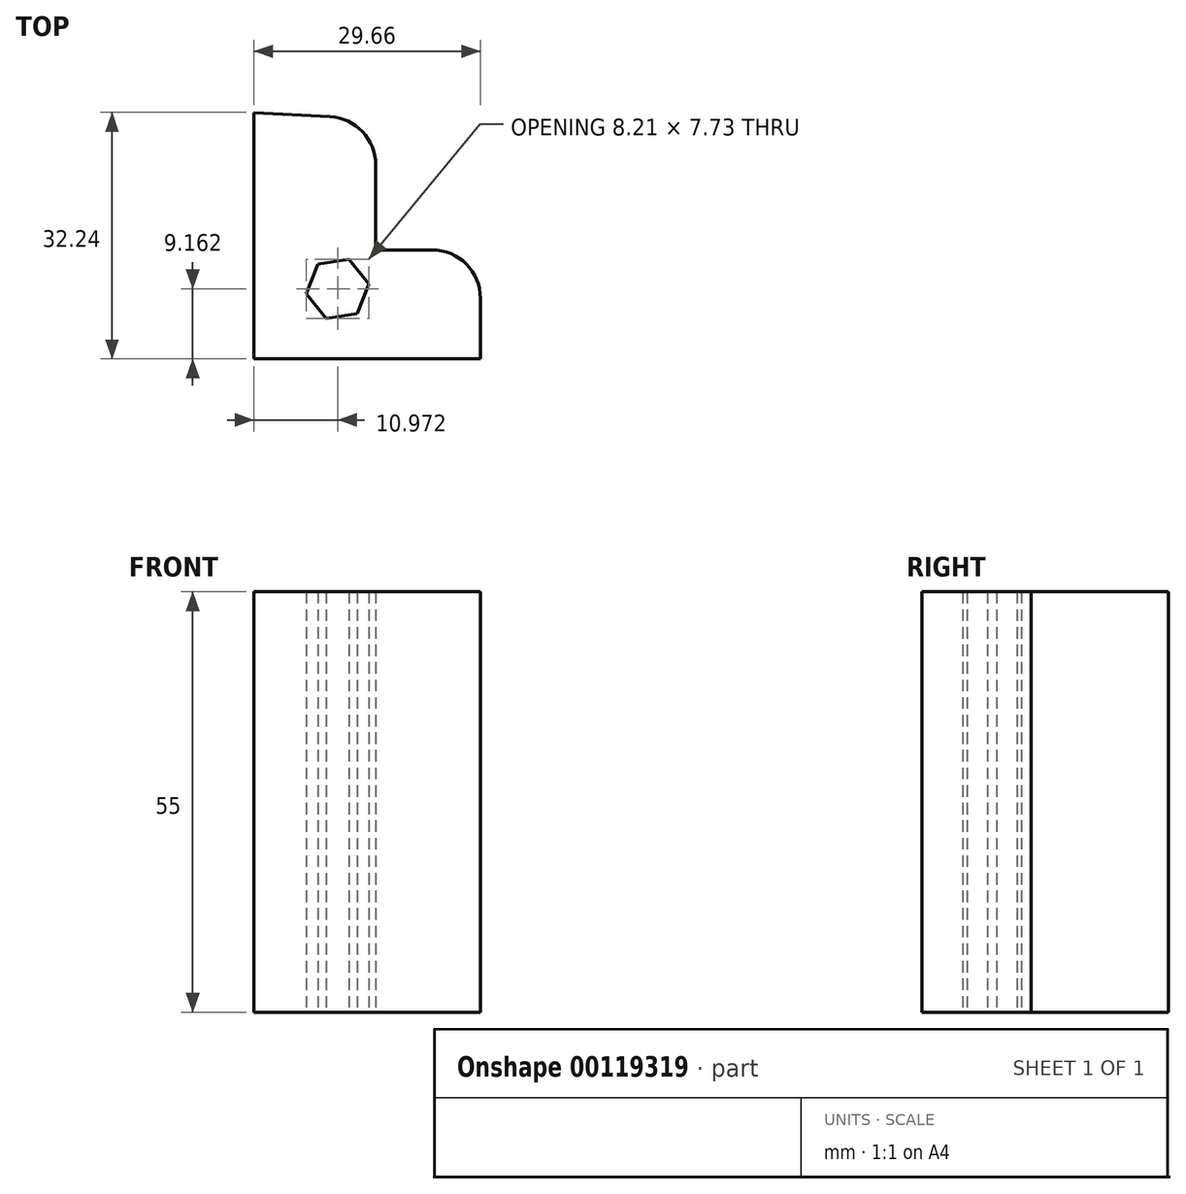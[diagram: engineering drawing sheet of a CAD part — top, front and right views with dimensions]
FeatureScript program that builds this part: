
annotation { "Feature Type Name" : "Feature", "Feature Type Description" : "" }
export const myFeature = defineFeature(function(context is Context, id is Id, definition is map)
    precondition{}
    {
        {
            var Q0;
            Q0=qCreatedBy(makeId("Top.planeOp"),FACE);
            var sketch = newSketch(context, id + "F0", { "sketchPlane" : qUnion([Q0])});
            skLineSegment(sketch, "E0", {"start": v(-55.05, 38.94) * mm, "end": v(-55.05, 6.7) * mm});
            skLineSegment(sketch, "E1", {"start": v(-55.05, 6.7) * mm, "end": v(-25.39, 6.7) * mm});
            skLineSegment(sketch, "E2", {"start": v(-25.39, 6.7) * mm, "end": v(-25.39, 14.62) * mm});
            skLineSegment(sketch, "E3", {"start": v(-31.74, 20.97) * mm, "end": v(-39.08, 20.97) * mm});
            skLineSegment(sketch, "E4", {"start": v(-39.08, 20.97) * mm, "end": v(-39.08, 32.06) * mm});
            skLineSegment(sketch, "E5", {"start": v(-45.09, 38.4) * mm, "end": v(-55.05, 38.94) * mm});
            skPoint(sketch, "E6.visualSharp", {"position": v(-39.08, 38.08) * mm});
            skArc(sketch, "E6.filletArc", {"start": v(-39.08, 32.06) * mm, "mid": v(-40.82, 36.43) * mm, "end": v(-45.09, 38.4) * mm});
            skPoint(sketch, "E7.visualSharp", {"position": v(-25.39, 20.97) * mm});
            skArc(sketch, "E7.filletArc", {"start": v(-25.39, 14.62) * mm, "mid": v(-27.25, 19.1) * mm, "end": v(-31.74, 20.97) * mm});
            skCircle(sketch, "E8.cCircle", {"center": v(-44.08, 15.86) * mm, "radius": 3.6 * mm, "construction": true});
            skLineSegment(sketch, "E8.0", {"start": v(-45.59, 12) * mm, "end": v(-48.18, 15.24) * mm});
            skLineSegment(sketch, "E8.1", {"start": v(-48.18, 15.24) * mm, "end": v(-46.67, 19.1) * mm});
            skLineSegment(sketch, "E8.2", {"start": v(-46.67, 19.1) * mm, "end": v(-42.57, 19.73) * mm});
            skLineSegment(sketch, "E8.3", {"start": v(-42.57, 19.73) * mm, "end": v(-39.97, 16.49) * mm});
            skLineSegment(sketch, "E8.4", {"start": v(-39.97, 16.49) * mm, "end": v(-41.48, 12.62) * mm});
            skLineSegment(sketch, "E8.5", {"start": v(-41.48, 12.62) * mm, "end": v(-45.59, 12) * mm});
            skPoint(sketch, "E8.0.midPoint", {"position": v(-46.89, 13.62) * mm});
            skSolve(sketch);
        }
        {
            var Q0;
            Q0 = qSketchRegion(id + "F0", true);
            extrude(context, id + "F1", {"entities" : qUnion([Q0]), "depth" : 25 * mm});
        }
        {
            var Q0;
            Q0 = qSketchRegion(id + "F0", true);
            var Q1;
            Q1=makeQuery(id+"F1.opExtrude","CAP_FACE",FACE,{"disambiguationData":[OSD([sQuery(id+"F0.wireOp",EDGE,"E0"),sQuery(id+"F0.wireOp",EDGE,"E1"),sQuery(id+"F0.wireOp",EDGE,"E2"),sQuery(id+"F0.wireOp",EDGE,"E3"),sQuery(id+"F0.wireOp",EDGE,"E4"),sQuery(id+"F0.wireOp",EDGE,"E5"),sQuery(id+"F0.wireOp",EDGE,"E6.filletArc"),sQuery(id+"F0.wireOp",EDGE,"E7.filletArc"),sQuery(id+"F0.wireOp",EDGE,"E8.0"),sQuery(id+"F0.wireOp",EDGE,"E8.1"),sQuery(id+"F0.wireOp",EDGE,"E8.2"),sQuery(id+"F0.wireOp",EDGE,"E8.3"),sQuery(id+"F0.wireOp",EDGE,"E8.4"),sQuery(id+"F0.wireOp",EDGE,"E8.5")])],"isStart":false});
            extrude(context, id + "F2", {"entities" : qUnion([Q0, Q1]), "operationType" : NewBodyOperationType.ADD, "depth" : 30 * mm});
        }
    });
